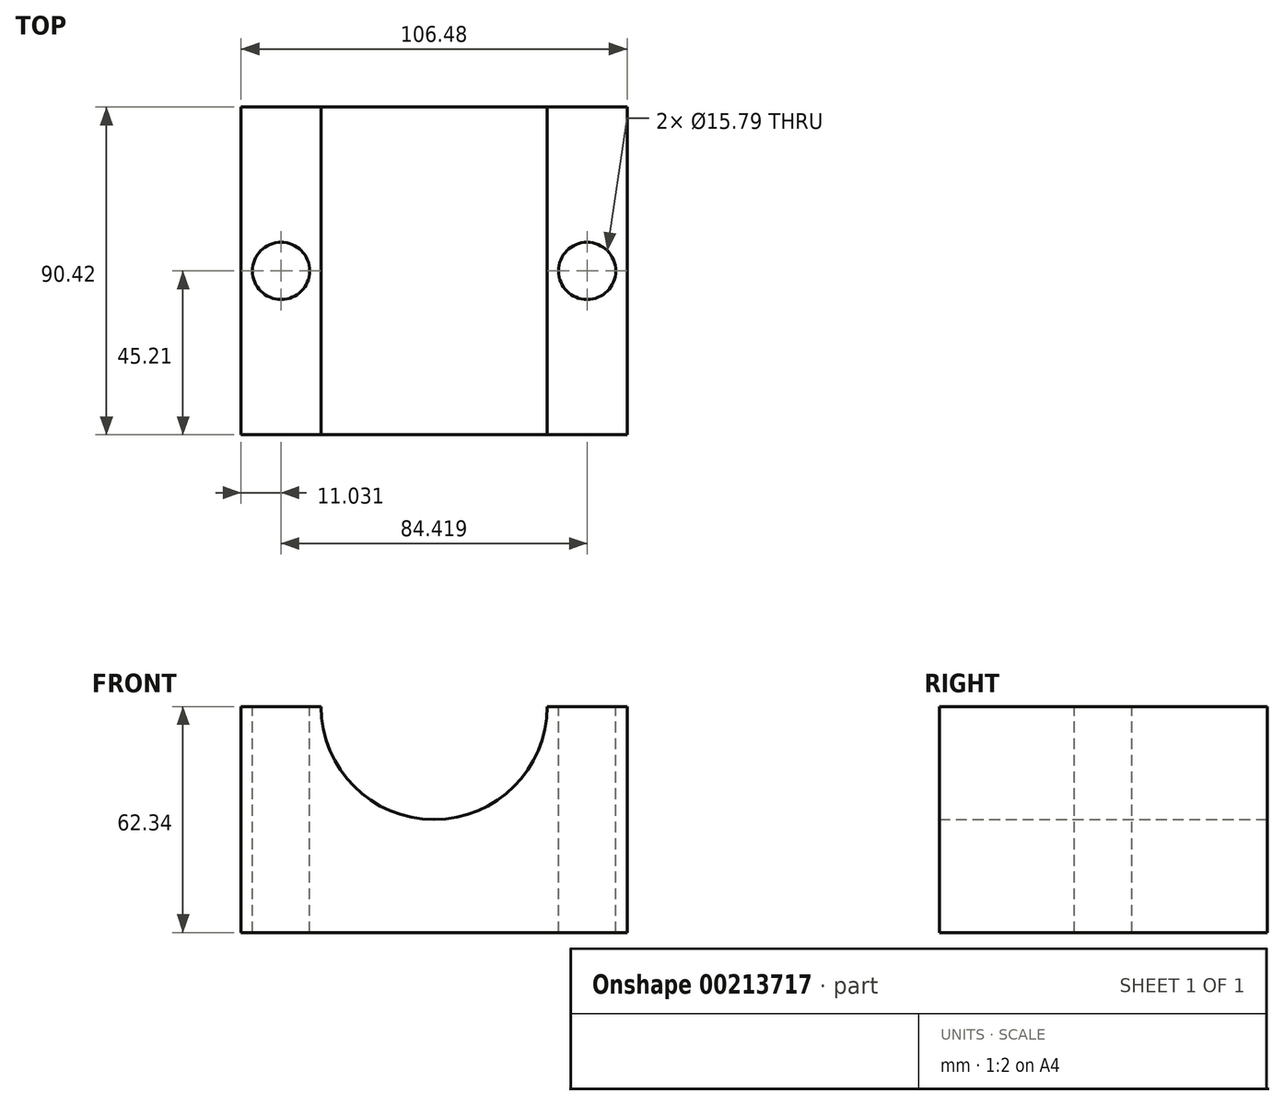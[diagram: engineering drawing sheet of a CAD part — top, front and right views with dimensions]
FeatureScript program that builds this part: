
annotation { "Feature Type Name" : "Feature", "Feature Type Description" : "" }
export const myFeature = defineFeature(function(context is Context, id is Id, definition is map)
    precondition{}
    {
        {
            var Q0;
            Q0=qCreatedBy(makeId("Front.planeOp"),FACE);
            var sketch = newSketch(context, id + "F0", { "sketchPlane" : qUnion([Q0])});
            skLineSegment(sketch, "E0.bottom", {"start": v(53.24, -31.17) * mm, "end": v(-53.24, -31.17) * mm});
            skLineSegment(sketch, "E0.top", {"start": v(53.24, 31.17) * mm, "end": v(-53.24, 31.17) * mm});
            skLineSegment(sketch, "E0.left", {"start": v(53.24, -31.17) * mm, "end": v(53.24, 31.17) * mm});
            skLineSegment(sketch, "E0.right", {"start": v(-53.24, -31.17) * mm, "end": v(-53.24, 31.17) * mm});
            skPoint(sketch, "E0.middle", {"position": v(0, 0) * mm});
            skCircle(sketch, "E1", {"center": v(0, 31.17) * mm, "radius": 31.17 * mm});
            skCircle(sketch, "E2", {"center": v(0, 31.17) * mm, "radius": 16.36 * mm});
            skSolve(sketch);
        }
        {
            var Q0;
            Q0=makeQuery(id+"F0.imprint","IMPRINT",FACE,{"disambiguationData":[TD([[makeQuery(id+"F0.imprint","IMPRINT",EDGE,{"derivedFrom":sQuery(id+"F0.wireOp",EDGE,"E0.bottom")}),-1.0]])]});
            var Q1;
            {var subQ0=sQuery(id+"F0.wireOp",EDGE,"E1");var subQ1=sQuery(id+"F0.wireOp",EDGE,"E0.top");var subQ2=makeQuery(id+"F0.imprint","INTERSECT",VERTEX,{"disambiguationData":[OD(0.0)],"derivedFrom":[subQ1,subQ0]});Q1=makeQuery(id+"F0.imprint","IMPRINT",FACE,{"disambiguationData":[TD([[makeQuery(id+"F0.imprint","IMPRINT",EDGE,{"disambiguationData":[TD([[subQ2,-1.0]])],"derivedFrom":subQ1}),1.0]])]});}
            extrude(context, id + "F1", {"entities" : qUnion([Q0, Q1]), "depth" : 59.94 * mm, "symmetric" : true});
        }
        {
            var Q0;
            {var subQ0=sQuery(id+"F0.wireOp",EDGE,"E1");var subQ1=sQuery(id+"F0.wireOp",EDGE,"E0.top");var subQ2=makeQuery(id+"F0.imprint","INTERSECT",VERTEX,{"disambiguationData":[OD(0.0)],"derivedFrom":[subQ1,subQ0]});Q0=makeQuery(id+"F0.imprint","IMPRINT",FACE,{"disambiguationData":[TD([[makeQuery(id+"F0.imprint","IMPRINT",EDGE,{"disambiguationData":[TD([[subQ2,-1.0]])],"derivedFrom":subQ1}),1.0]])]});}
            extrude(context, id + "F2", {"entities" : qUnion([Q0]), "operationType" : NewBodyOperationType.ADD, "depth" : 90.42 * mm, "symmetric" : true});
        }
        {
            var Q0;
            {var subQ0=sQuery(id+"F0.wireOp",EDGE,"E0.top");var subQ1=makeQuery(id+"F0.imprint","INTERSECT",VERTEX,{"disambiguationData":[OD(0.0)],"derivedFrom":[subQ0,sQuery(id+"F0.wireOp",EDGE,"E1")]});var subQ2=makeQuery(id+"F0.imprint","IMPRINT",EDGE,{"disambiguationData":[TD([[subQ1,-1.0]])],"derivedFrom":subQ0});Q0=makeQuery(id+"F2.boolean.opBoolean","MERGE",FACE,{"derivedFrom":[makeQuery(id+"F1.opExtrude","SWEPT_FACE",FACE,{"disambiguationData":[OSD([subQ0]),TDD([makeQuery(id+"F0.imprint","IMPRINT",EDGE,{"disambiguationData":[TD([[makeQuery(id+"F0.imprint","INTERSECT",VERTEX,{"derivedFrom":[subQ0,sQuery(id+"F0.wireOp",EDGE,"E0.left")]}),-1.0]])],"derivedFrom":subQ0}),subQ2])]}),makeQuery(id+"F2.opExtrude","SWEPT_FACE",FACE,{"disambiguationData":[OSD([subQ0]),TDD([subQ2])]})]});}
            var sketch = newSketch(context, id + "F3", { "sketchPlane" : qUnion([Q0])});
            skCircle(sketch, "E3", {"center": v(42.2, 0) * mm, "radius": 7.9 * mm});
            skCircle(sketch, "E4", {"center": v(-42.2, 0) * mm, "radius": 7.9 * mm});
            skSolve(sketch);
        }
        {
            var Q0;
            Q0 = qSketchRegion(id + "F3", true);
            extrude(context, id + "F4", {"entities" : qUnion([Q0]), "operationType" : NewBodyOperationType.REMOVE, "endBound" : BoundingType.THROUGH_ALL, "oppositeDirection" : true, "depth" : 25.4 * mm});
        }
    });
